# Revit family: Detectable-Warning-Surfaces_Cast-Iron-Dome-24x24_ADA-Solutions
name_source: partatom
category: Generic Models
units: mm (PartAtom-declared; Revit-internal decimal feet)

## family parameters
Always vertical = Yes
Can host rebar = No
Cut with Voids When Loaded = No
Host = Floor
Maintain Annotation Orientation = No
Part Type = Normal
Room Calculation Point = No
Round Connector Dimension = Use Diameter
Shared = No

## types (9) — shared parameters
Default Elevation = 0"
Keynote = 09 33 00
Length = 24"
Manufacturer = ADA Solutions
Model = Iron Dome Cast Iron
Product Page URL = https://www.arcat.com
URL = https://adatile.com
Width = 24"

## per-type parameters (varying)
| type | Color |
| ADA Dark Gray | ADA Dark Gray |
| ADA Black | ADA Black |
| ADA Blue | ADA Blue |
| ADA Yellow | ADA Yellow |
| ADA Seatle Yellow | ADA Seattle Yellow |
| ADA White | ADA White |
| ADA Safety Red | ADA Safety Red |
| ADA Brick Red | ADA Brick Red |
| ADA Clay Red | ADA Clay Red |

## geometry (parser evidence)
native form markers: Sweep x3
no freeform markers — native parametric forms only
